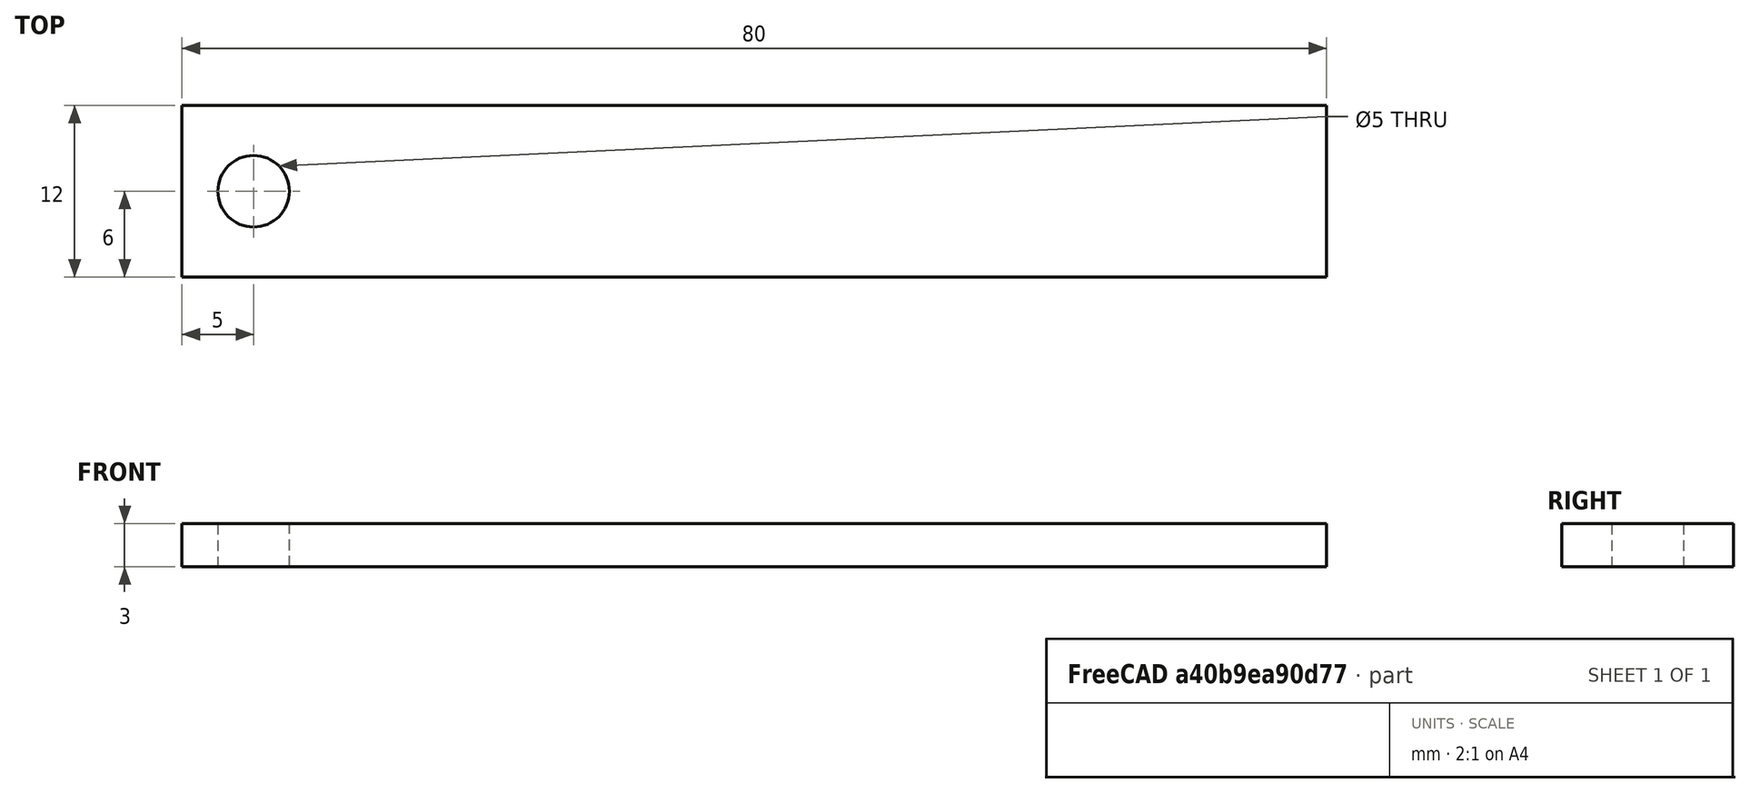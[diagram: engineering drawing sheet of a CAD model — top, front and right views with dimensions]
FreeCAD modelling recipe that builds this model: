
FCSTD DOCUMENT  (FreeCAD 1.0R39319 (Git))
Label: rec part
License: All rights reserved
LicenseURL: https://en.wikipedia.org/wiki/All_rights_reserved
objects: Part::Extrusion×2, Sketcher::SketchObject×1
note: 4 computed .brp shape members not serialized (recipe doc carries the construction recipe); baked Part::Feature solids carry a one-line shape summary decoded from their .brp

FEATURE [Sketcher::SketchObject] Sketch
  ArcFitTolerance = 1e-06
  FullyConstrained = true
  MakeInternals = false
  sketch-geometry (6):
    g0: LineSegment StartX=-40 StartY=6 StartZ=0 EndX=-40 EndY=-6 EndZ=0
    g1: LineSegment StartX=-40 StartY=-6 StartZ=0 EndX=40 EndY=-6 EndZ=0
    g2: LineSegment StartX=40 StartY=-6 StartZ=0 EndX=40 EndY=6 EndZ=0
    g3: LineSegment StartX=40 StartY=6 StartZ=0 EndX=-40 EndY=6 EndZ=0
    g4: GeomPoint [constr] X=0 Y=0 Z=0
    g5: Circle CenterX=-35 CenterY=0 CenterZ=0 NormalX=0 NormalY=0 NormalZ=1 AngleXU=0 Radius=2.5
  constraints (15):
    c: Coincident(g0,g1)
    c: Coincident(g1,g2)
    c: Coincident(g2,g3)
    c: Coincident(g3,g0)
    c: Vertical(g0)
    c: Vertical(g2)
    c: Horizontal(g1)
    c: Horizontal(g3)
    c: Symmetric(g2,g0,g4)
    c: Coincident(g4,g-1)
    c: DistanceX(g3,g3) = 80
    c: DistanceY(g0,g0) = 12
    c: PointOnObject(g5,g-1)
    c: Diameter(g5) = 5
    c: Distance(g5,g0) = 5
FEATURE [Part::Extrusion] Extrude
  Base = -> Sketch
  Dir = (0,0,1)
  DirMode = 2
  FaceMakerClass = Part::FaceMakerBullseye
  FaceMakerMode = 3
  LengthFwd = 3
  LengthRev = 0
  Solid = true
  Symmetric = false
FEATURE [Part::Extrusion] Extrude001
  Base = -> Sketch
  Dir = (0,0,1)
  DirMode = 2
  FaceMakerClass = Part::FaceMakerBullseye
  FaceMakerMode = 3
  LengthFwd = 3
  LengthRev = 0
  Solid = true
  Symmetric = false
